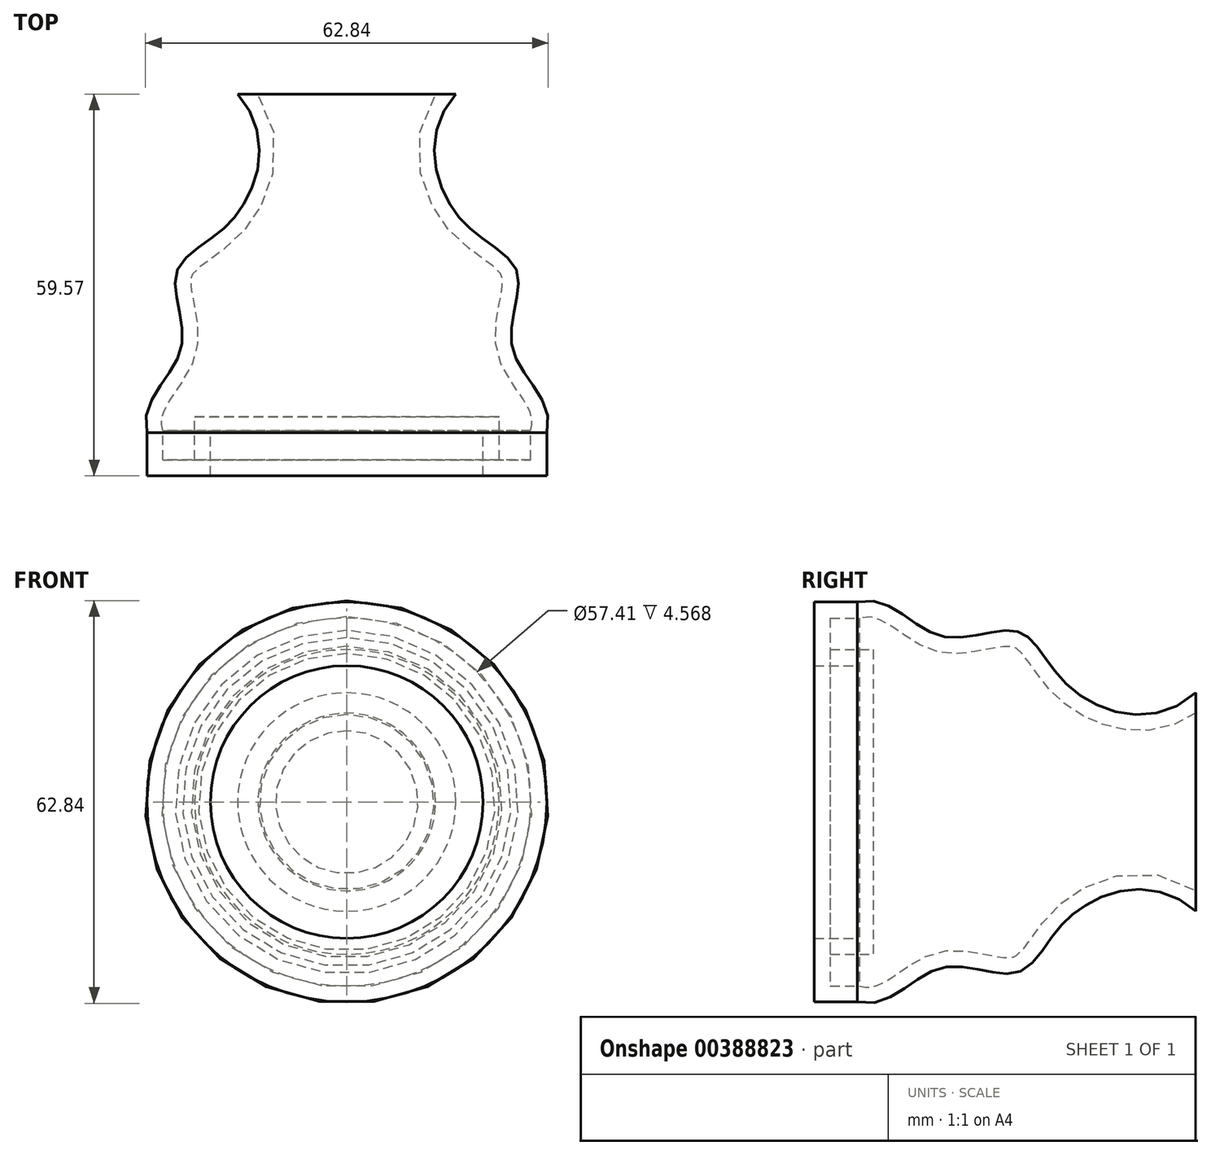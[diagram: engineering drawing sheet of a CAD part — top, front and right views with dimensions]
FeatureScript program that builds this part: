
annotation { "Feature Type Name" : "Feature", "Feature Type Description" : "" }
export const myFeature = defineFeature(function(context is Context, id is Id, definition is map)
    precondition{}
    {
        {
            var Q0;
            Q0=qCreatedBy(makeId("Top.planeOp"),FACE);
            var sketch = newSketch(context, id + "F0", { "sketchPlane" : qUnion([Q0])});
            skLineSegment(sketch, "E0", {"start": v(17.04, 0) * mm, "end": v(0, 0) * mm});
            skLineSegment(sketch, "E1", {"start": v(0, 0) * mm, "end": v(0, -52.84) * mm});
            skLineSegment(sketch, "E2", {"start": v(0, -52.84) * mm, "end": v(21.28, -52.84) * mm});
            skLineSegment(sketch, "E3", {"start": v(21.28, -52.84) * mm, "end": v(21.28, -59.57) * mm});
            skLineSegment(sketch, "E4", {"start": v(21.28, -59.57) * mm, "end": v(31.2, -59.57) * mm});
            skLineSegment(sketch, "E5", {"start": v(31.2, -59.57) * mm, "end": v(31.2, -52.84) * mm});
            skFitSpline(sketch, "E6", {"points": [v(17.04, 0) * mm, v(18.09, -19.86) * mm, v(26.6, -27.8) * mm, v(25.92, -39.9) * mm, v(31.2, -52.84) * mm], "startDerivative": vector(-59.43, -66.74) * mm, "endDerivative": vector(-16.55, -61.61) * mm});
            skSolve(sketch);
        }
        {
            var Q0;
            Q0=makeQuery(id+"F0.imprint","IMPRINT",FACE,{"disambiguationData":[TD([[makeQuery(id+"F0.imprint","IMPRINT",EDGE,{"derivedFrom":sQuery(id+"F0.wireOp",EDGE,"E0")}),1.0]])]});
            var Q1;
            Q1=sQuery(id+"F0.wireOp",EDGE,"E1");
            revolve(context, id + "F1", {"entities" : qUnion([Q0]), "axis" : qUnion([Q1]), "revolveType" : RevolveType.FULL});
        }
        {
            var Q0;
            Q0=makeQuery(id+"F1.opRevolve","SWEPT_FACE",FACE,{"disambiguationData":[OSD([sQuery(id+"F0.wireOp",EDGE,"E0")])]});
            shell(context, id + "F2", {"entities" : qUnion([Q0]), "thickness" : 2.5 * mm});
        }
    });
